# Revit family: 455940001_Grifería Lavaplatos Nogal Sencilla
name_source: partatom
category: Plumbing Fixtures
units: mm (PartAtom-declared; Revit-internal decimal feet)

## family parameters
Cut with Voids When Loaded = No
Host = Face
OmniClass Number = 23.31.11.00
OmniClass Title = Faucets
Part Type = Normal
Room Calculation Point = No
Round Connector Dimension = Use Diameter
Shared = No

## types (1)
- 455940001_Lavaplatos_Sencillo_Nogal
    Alto = 389 mm
    Ancho = 101 mm
    Capacidad de flujo = A 60 psi: 4.88 L/min.
    Ciclo de vida de la unidad de cierre = 500000 ciclos.
    Creado por = BIMBAU.
    Default Elevation = 0 mm  [stored 0 ft]
    Description = La gr´fería de cocina Nogal ha sido diseñada para trabaja en perfecta armonía con el espacio; inspirada en las necesidades del consumidor latinoamericano dando como resultado un producto robusto y funcional.
    Dimensiones generales del producto = 345 x 139 x 221 mm.
    Diámetro abasto = 13 mm  [stored 0.0426509 ft]
    Fecha de creación = 09/04/2021.
    Garantía = 30 años Grival - 5 años Cromado.
    Manufacturer = Corona.
    Material = Corona_Cromado
    Material 2 = Corona_Acero inoxidable
    Model = 455940001_Lavaplatos_Sencillo_Nogal
    Normatividad = NTC 1644.
    Peso  Bruto = 325 gr. / 0.72 lb.
    Peso neto = 305 gr. / 0.67 lb.
    Presión máxima recomendada = 125 psi.
    Presión mínima recomendada = 20 psi.
    Profundidad = 248 mm
    Recubrimientos = Resistente a la corrosión, pelado y decoloración por agua. Recubrimientos no tóxicos. Producto para uso doméstico.
    Temperaturas máxima de trabajo = 71° C / 159.8° F.
    Temperaturas mínima de trabajo = 5° C / 41° F.

note: [stored X ft] marks values corroborated as IEEE doubles in the binary element streams (Revit-internal decimal feet)

## geometry (parser evidence)
native form markers: Sweep x5
no freeform markers — native parametric forms only
